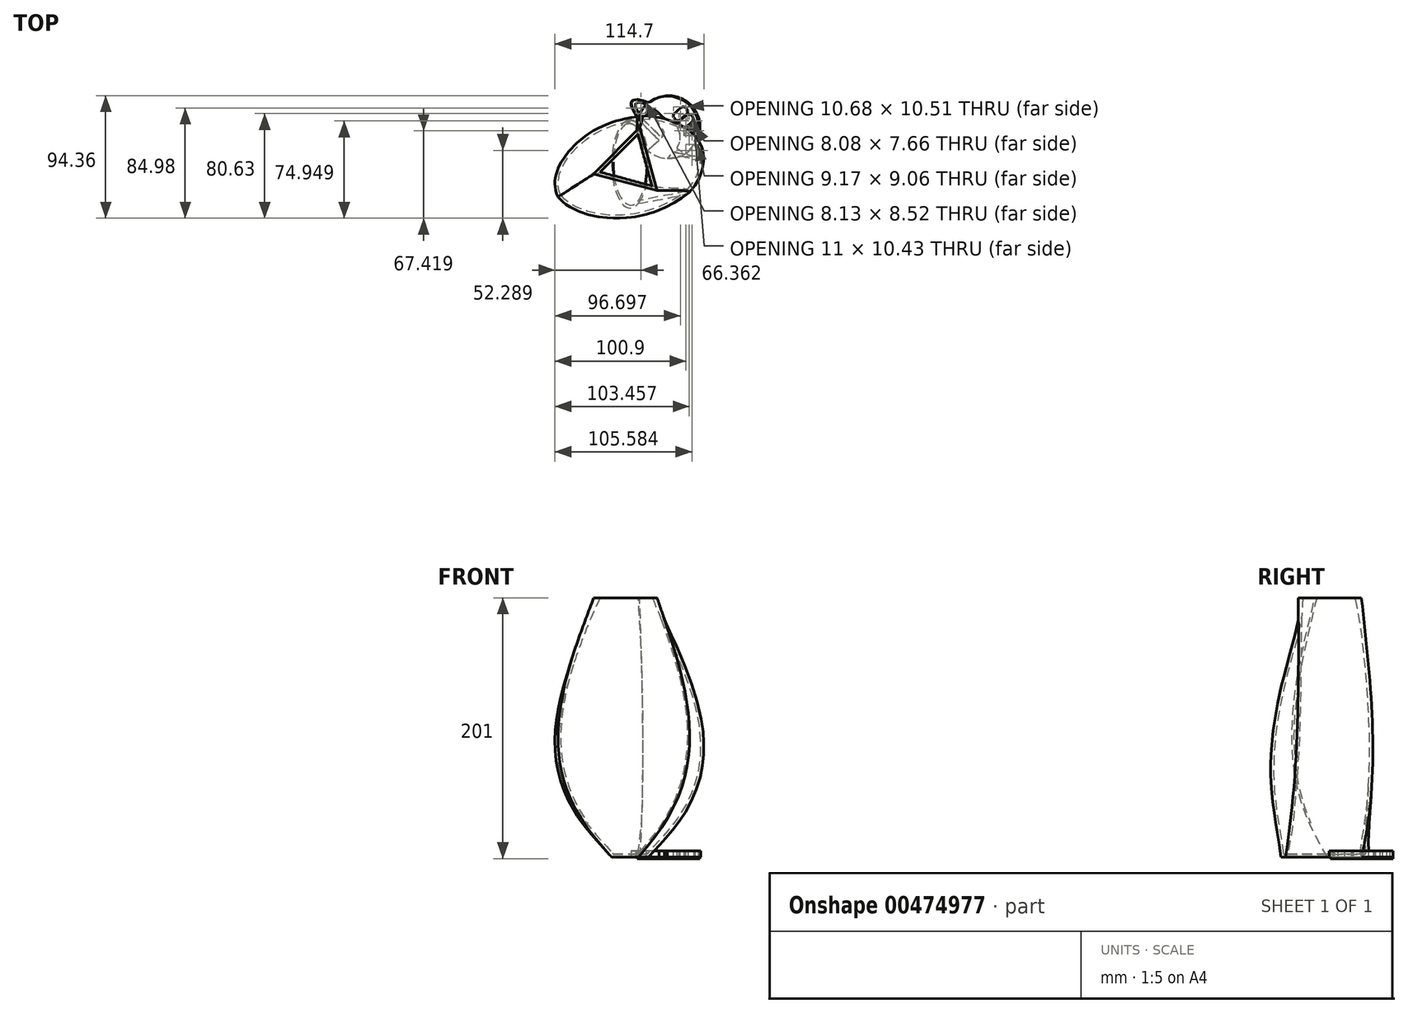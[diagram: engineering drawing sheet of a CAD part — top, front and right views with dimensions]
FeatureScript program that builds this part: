
annotation { "Feature Type Name" : "Feature", "Feature Type Description" : "" }
export const myFeature = defineFeature(function(context is Context, id is Id, definition is map)
    precondition{}
    {
        {
            var Q0;
            Q0=qCreatedBy(makeId("Top.planeOp"),FACE);
            var sketch = newSketch(context, id + "F0", { "sketchPlane" : qUnion([Q0])});
            skFitSpline(sketch, "E0", {"points": [v(24.4, 20.38) * mm, v(26.33, 23.66) * mm, v(22.86, 29.26) * mm, v(20.86, 34.15) * mm, v(15.78, 38.08) * mm, v(12.88, 38.14) * mm, v(12.1, 38.98) * mm, v(15.32, 41.68) * mm, v(19.12, 41.68) * mm, v(26.91, 34.8) * mm, v(31.29, 33.25) * mm, v(37.28, 26.43) * mm, v(38.24, 20.25) * mm, v(37.73, 15.74) * mm, v(35.96, 12.26) * mm, v(35.99, 12.2) * mm, v(41.86, 8.46) * mm, v(41.87, 8.44) * mm, v(39.56, 7.18) * mm, v(39.4, 7.18) * mm, v(34.32, 9.82) * mm, v(32.7, 8.47) * mm, v(28.59, 4.54) * mm, v(34.57, 5.12) * mm, v(39.6, 6.66) * mm, v(42.68, 5.31) * mm, v(48.22, 3.7) * mm, v(50.47, 3.32) * mm, v(52.92, 3.96) * mm, v(54.2, 6.86) * mm, v(53.5, 10.14) * mm, v(51.76, 14.07) * mm, v(50.22, 16.38) * mm, v(49.83, 16.77) * mm, v(51.25, 19.54) * mm, v(52.53, 25.65) * mm, v(52.73, 31.06) * mm, v(51.47, 36.4) * mm, v(48.87, 41.49) * mm, v(44.86, 46.36) * mm, v(38.26, 50.36) * mm, v(31.55, 52.31) * mm, v(24.4, 51.77) * mm, v(18.34, 49.93) * mm, v(14.44, 47.55) * mm, v(13.57, 47.44) * mm, v(12.6, 47.98) * mm, v(7.4, 49.71) * mm, v(2.86, 49.5) * mm, v(1.02, 48.2) * mm, v(1.23, 43.98) * mm, v(5.78, 35.31) * mm, v(5.56, 34.56) * mm, v(5.45, 32.07) * mm, v(5.24, 25.68) * mm, v(6.86, 19.3) * mm, v(9.03, 15.07) * mm, v(13.03, 10.2) * mm, v(13.8, 10.2) * mm, v(14.22, 11.06) * mm, v(22.13, 18.32) * mm, v(22.24, 18.75) * mm, v(21.59, 19.18) * mm, v(13.36, 27.2) * mm, v(7.08, 34.34) * mm, v(6.65, 35.42) * mm, v(7.08, 37.37) * mm, v(10.43, 33.9) * mm, v(10.48, 33.85) * mm, v(24.4, 20.38) * mm, v(24.4, 20.38) * mm]});
            skFitSpline(sketch, "E1", {"points": [v(35.82, 33.64) * mm, v(34.11, 35.23) * mm, v(33.23, 36.61) * mm, v(33.32, 37.94) * mm, v(34.3, 39.21) * mm, v(40.04, 44.01) * mm, v(40.4, 44.1) * mm, v(41.28, 44.15) * mm, v(42.22, 43.73) * mm, v(44.4, 41.09) * mm, v(44.25, 39.64) * mm, v(43.98, 39.22) * mm, v(37.7, 33.67) * mm, v(36.96, 33.5) * mm, v(35.82, 33.64) * mm]});
            skFitSpline(sketch, "E2", {"points": [v(39.86, 28) * mm, v(37.6, 30.46) * mm, v(37.49, 31.86) * mm, v(37.93, 32.95) * mm, v(38.11, 33.1) * mm, v(44.31, 38.25) * mm, v(44.36, 38.24) * mm, v(45.96, 38.36) * mm, v(48.64, 35.37) * mm, v(48.5, 33.65) * mm, v(41.98, 27.86) * mm, v(41.7, 27.72) * mm, v(39.86, 28) * mm]});
            skFitSpline(sketch, "E3", {"points": [v(45.37, 29.5) * mm, v(46.37, 29.68) * mm, v(47.38, 29.34) * mm, v(49.51, 27) * mm, v(49.5, 26.03) * mm, v(49.43, 25.11) * mm, v(45.76, 21.89) * mm, v(44.72, 21.73) * mm, v(43.72, 21.83) * mm, v(41.65, 23.99) * mm, v(41.31, 24.96) * mm, v(41.45, 26.05) * mm, v(45.37, 29.5) * mm]});
            skFitSpline(sketch, "E4", {"points": [v(12.48, 45.8) * mm, v(9.71, 42.7) * mm, v(7.31, 38.8) * mm, v(7.13, 38.74) * mm, v(6.88, 39.01) * mm, v(4.84, 42.74) * mm, v(4.22, 44.8) * mm, v(4.56, 46.73) * mm, v(6.05, 47.44) * mm, v(8.56, 47.33) * mm, v(11.93, 46.08) * mm, v(12.48, 45.8) * mm]});
            skFitSpline(sketch, "E5", {"points": [v(48.97, 15.08) * mm, v(51.74, 10.36) * mm, v(52.25, 7.77) * mm, v(51.64, 6.56) * mm, v(50.35, 5.97) * mm, v(46.36, 6.6) * mm, v(43, 8) * mm, v(42.8, 8.26) * mm, v(42.84, 8.68) * mm, v(45.9, 11.37) * mm, v(48.68, 14.67) * mm, v(48.97, 15.08) * mm]});
            skSolve(sketch);
        }
        {
            var Q0;
            Q0 = qSketchRegion(id + "F0", true);
            extrude(context, id + "F1", {"entities" : qUnion([Q0]), "depth" : 5 * mm});
        }
        {
            var Q0;
            Q0=qCreatedBy(makeId("Top.planeOp"),FACE);
            var sketch = newSketch(context, id + "F2", { "sketchPlane" : qUnion([Q0])});
            skPoint(sketch, "E6.0", {"position": v(27.5, 55) * mm});
            skPoint(sketch, "E7.0", {"position": v(5.24, 25.68) * mm});
            skPoint(sketch, "E7.1", {"position": v(52.73, 31.06) * mm});
            skPoint(sketch, "E7.2", {"position": v(24.4, 51.77) * mm});
            skPoint(sketch, "E7.3", {"position": v(34.57, 5.12) * mm});
            skLineSegment(sketch, "E8", {"start": v(24.4, 51.77) * mm, "end": v(34.57, 5.12) * mm, "construction": true});
            skLineSegment(sketch, "E9", {"start": v(5.24, 25.68) * mm, "end": v(52.73, 31.06) * mm, "construction": true});
            skPoint(sketch, "E10", {"position": v(29.64, 28.44) * mm});
            skPoint(sketch, "E10.positionSnap0", {"position": v(29.49, 28.44) * mm});
            skCircle(sketch, "E11", {"center": v(29.64, 28.44) * mm, "radius": 24.18 * mm});
            skSolve(sketch);
        }
        {
            var Q0;
            Q0=makeQuery(id+"F2.imprint","IMPRINT",FACE,{"disambiguationData":[TD([[makeQuery(id+"F2.imprint","IMPRINT",EDGE,{"derivedFrom":sQuery(id+"F2.wireOp",EDGE,"E11")}),1.0]])]});
            var Q1;
            Q1=sQuery(id+"F2.wireOp",EDGE,"E11");
            extrude(context, id + "F3", {"entities" : qUnion([Q0]), "surfaceEntities" : qUnion([Q1]), "oppositeDirection" : true, "depth" : 1 * mm});
        }
        {
            var Q0;
            Q0=qCreatedBy(makeId("Top.planeOp"),FACE);
            var sketch = newSketch(context, id + "F4", { "sketchPlane" : qUnion([Q0])});
            skEllipse(sketch, "E12", {"center": v(0, 0) * mm, "majorRadius": 33.96 * mm, "minorRadius": 14.14 * mm, "majorAxis": v(0, 1)});
            skSolve(sketch);
        }
        {
            var Q0;
            Q0=qCreatedBy(makeId("Top.planeOp"),FACE);
            cPlane(context, id + "F5", {"entities" : qUnion([Q0]), "cplaneType" : CPlaneType.OFFSET, "offset" : 200 * mm, "width" : 150 * mm, "height" : 150 * mm});
        }
        {
            var Q0;
            Q0=qCreatedBy(makeId("Top.planeOp"),FACE);
            cPlane(context, id + "F6", {"entities" : qUnion([Q0]), "cplaneType" : CPlaneType.OFFSET, "offset" : 25 * mm, "width" : 150 * mm, "height" : 150 * mm});
        }
        {
            var Q0;
            Q0=qCreatedBy(id+"F6.planeOp",FACE);
            var sketch = newSketch(context, id + "F7", { "sketchPlane" : qUnion([Q0])});
            skPoint(sketch, "E13.0", {"position": v(0, 0) * mm});
            skCircle(sketch, "E14", {"center": v(0, -1.78) * mm, "radius": 35.83 * mm});
            skSolve(sketch);
        }
        {
            var Q0;
            Q0=qCreatedBy(id+"F5.planeOp",FACE);
            var sketch = newSketch(context, id + "F8", { "sketchPlane" : qUnion([Q0])});
            skPoint(sketch, "E15.0", {"position": v(0, 0) * mm});
            skCircle(sketch, "E16.cCircle", {"center": v(0, 0) * mm, "radius": 29.1 * mm, "construction": true});
            skLineSegment(sketch, "E16.0", {"start": v(7.36, 28.15) * mm, "end": v(20.7, -20.45) * mm});
            skLineSegment(sketch, "E16.1", {"start": v(20.7, -20.45) * mm, "end": v(-28.06, -7.7) * mm});
            skLineSegment(sketch, "E16.2", {"start": v(-28.06, -7.7) * mm, "end": v(7.36, 28.15) * mm});
            skSolve(sketch);
        }
        {
            var Q0;
            Q0=makeQuery(id+"F4.imprint","IMPRINT",FACE,{"disambiguationData":[TD([[makeQuery(id+"F4.imprint","IMPRINT",EDGE,{"derivedFrom":sQuery(id+"F4.wireOp",EDGE,"E12")}),1.0]])]});
            var Q1;
            Q1=makeQuery(id+"F7.imprint","IMPRINT",FACE,{"disambiguationData":[TD([[makeQuery(id+"F7.imprint","IMPRINT",EDGE,{"derivedFrom":sQuery(id+"F7.wireOp",EDGE,"E14")}),1.0]])]});
            var Q2;
            Q2=makeQuery(id+"F8.imprint","IMPRINT",FACE,{"disambiguationData":[TD([[makeQuery(id+"F8.imprint","IMPRINT",EDGE,{"derivedFrom":sQuery(id+"F8.wireOp",EDGE,"E16.0")}),-1.0]])]});
            loft(context, id + "F9", {"sheetProfilesArray" : [{ "sheetProfileEntities" : qUnion([Q0]) }, { "sheetProfileEntities" : qUnion([Q1]) }, { "sheetProfileEntities" : qUnion([Q2]) }]});
        }
        {
            var Q0;
            Q0=makeQuery(id+"F9.opLoft","CAP_FACE",FACE,{"disambiguationData":[OSD([makeQuery(id+"F8.imprint","IMPRINT",FACE,{"disambiguationData":[TD([[makeQuery(id+"F8.imprint","IMPRINT",EDGE,{"derivedFrom":sQuery(id+"F8.wireOp",EDGE,"E16.0")}),-1.0]])]})])],"isStart":true});
            shell(context, id + "F10", {"entities" : qUnion([Q0]), "thickness" : 2.5 * mm});
        }
    });
